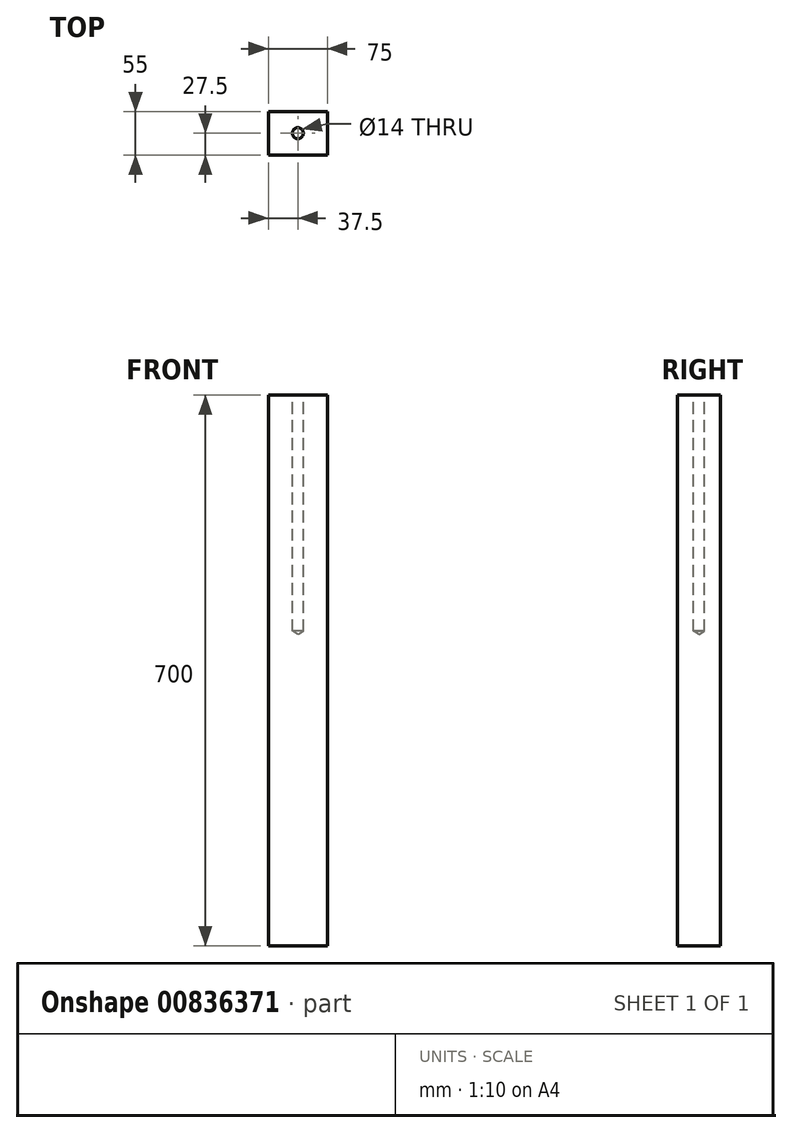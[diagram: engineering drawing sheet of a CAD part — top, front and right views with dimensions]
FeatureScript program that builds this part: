
annotation { "Feature Type Name" : "Feature", "Feature Type Description" : "" }
export const myFeature = defineFeature(function(context is Context, id is Id, definition is map)
    precondition{}
    {
        {
            var Q0;
            Q0=qCreatedBy(makeId("Top.planeOp"),FACE);
            var sketch = newSketch(context, id + "F0", { "sketchPlane" : qUnion([Q0])});
            skLineSegment(sketch, "E0.bottom", {"start": v(0, 0) * mm, "end": v(75, 0) * mm});
            skLineSegment(sketch, "E0.top", {"start": v(0, 55) * mm, "end": v(75, 55) * mm});
            skLineSegment(sketch, "E0.left", {"start": v(0, 0) * mm, "end": v(0, 55) * mm});
            skLineSegment(sketch, "E0.right", {"start": v(75, 0) * mm, "end": v(75, 55) * mm});
            skSolve(sketch);
        }
        {
            var Q0;
            Q0=makeQuery(id+"F0.imprint","IMPRINT",FACE,{"disambiguationData":[TD([[makeQuery(id+"F0.imprint","IMPRINT",EDGE,{"derivedFrom":sQuery(id+"F0.wireOp",EDGE,"E0.bottom")}),1.0]])]});
            extrude(context, id + "F1", {"entities" : qUnion([Q0]), "depth" : 700 * mm, "offsetDistance" : 25 * mm});
        }
        {
            var Q0;
            Q0=makeQuery(id+"F1.opExtrude","CAP_FACE",FACE,{"disambiguationData":[OSD([sQuery(id+"F0.wireOp",EDGE,"E0.bottom"),sQuery(id+"F0.wireOp",EDGE,"E0.top"),sQuery(id+"F0.wireOp",EDGE,"E0.left"),sQuery(id+"F0.wireOp",EDGE,"E0.right")])],"isStart":false});
            var sketch = newSketch(context, id + "F2", { "sketchPlane" : qUnion([Q0])});
            skLineSegment(sketch, "E1", {"start": v(0, 55) * mm, "end": v(75, 0) * mm});
            skLineSegment(sketch, "E2", {"start": v(75, 0) * mm, "end": v(75, 55) * mm});
            skLineSegment(sketch, "E3", {"start": v(75, 55) * mm, "end": v(0, 0) * mm});
            skCircle(sketch, "E4", {"center": v(37.5, 27.5) * mm, "radius": 7 * mm});
            skLineSegment(sketch, "E5", {"start": v(37.5, 27.5) * mm, "end": v(38.04, 34.48) * mm});
            skSolve(sketch);
        }
        {
            var Q0;
            Q0=sQuery(id+"F2.wireOp",VERTEX,"E5.start");
            var Q1;
            Q1=makeQuery(id+"F1.opExtrude","SWEPT_BODY",BODY,{"disambiguationData":[OSD([sQuery(id+"F0.wireOp",EDGE,"E0.bottom"),sQuery(id+"F0.wireOp",EDGE,"E0.top"),sQuery(id+"F0.wireOp",EDGE,"E0.left"),sQuery(id+"F0.wireOp",EDGE,"E0.right")])]});
            hole(context, id + "F3", {"style" : HoleStyle.SIMPLE, "endStyle" : HoleEndStyle.BLIND, "holeDiameter" : 14 * mm, "majorDiameter" : 5 * mm, "holeDepth" : 300 * mm, "isTappedThrough" : true, "tappedDepth" : 12 * mm, "tapClearance" : 3, "locations" : qUnion([Q0]), "scope" : qUnion([Q1])});
        }
    });
